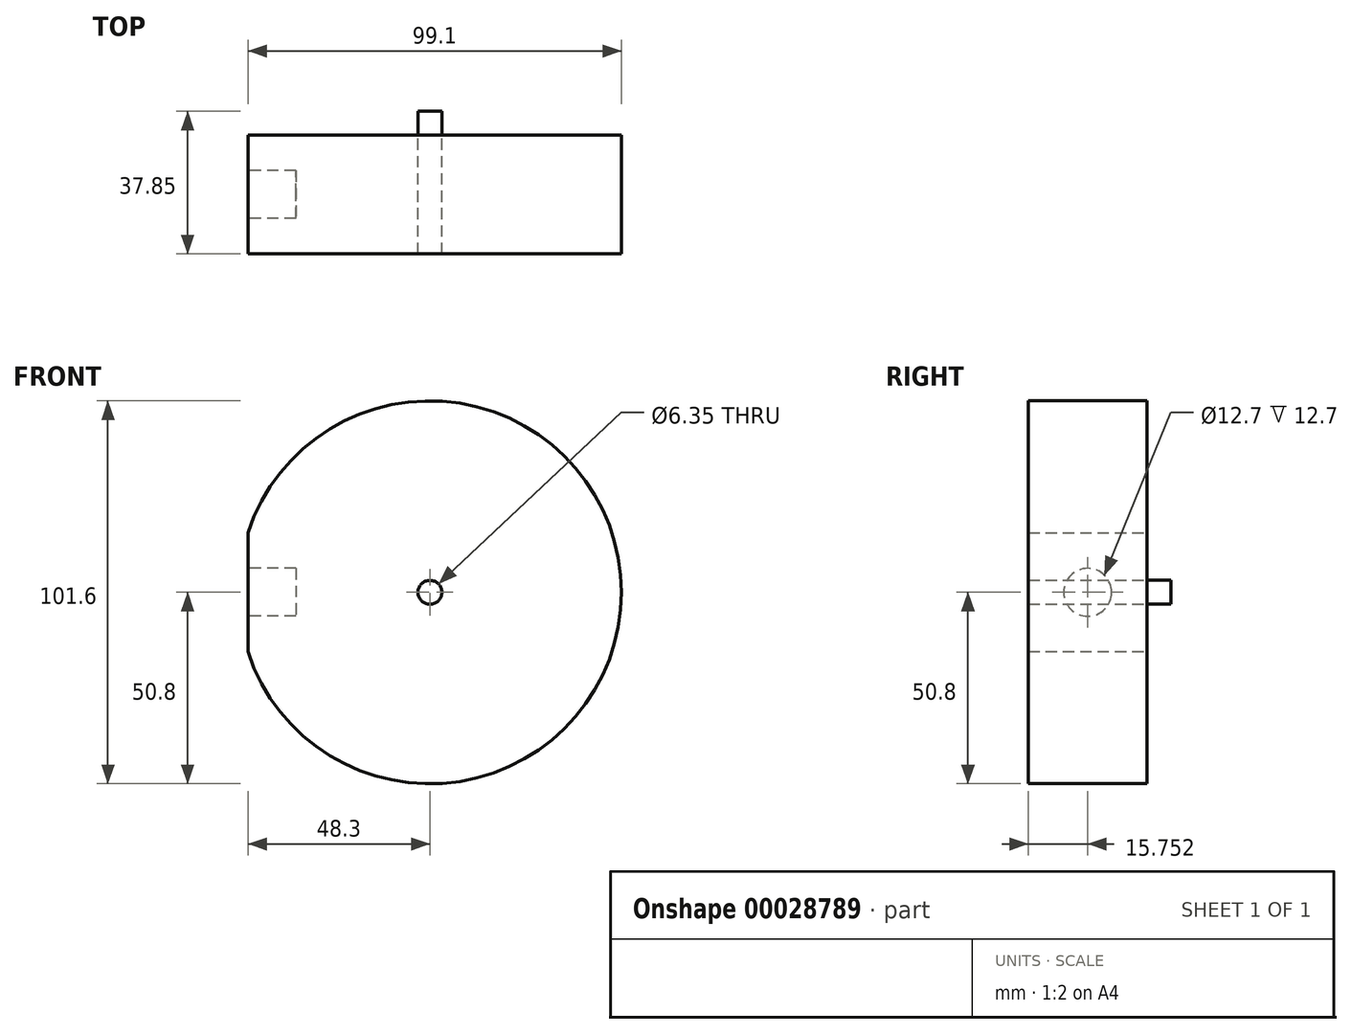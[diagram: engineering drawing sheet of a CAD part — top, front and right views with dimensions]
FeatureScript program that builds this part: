
annotation { "Feature Type Name" : "Feature", "Feature Type Description" : "" }
export const myFeature = defineFeature(function(context is Context, id is Id, definition is map)
    precondition{}
    {
        {
            var Q0;
            Q0=qCreatedBy(makeId("Front.planeOp"),FACE);
            var sketch = newSketch(context, id + "F0", { "sketchPlane" : qUnion([Q0])});
            skArc(sketch, "E0", {"start": v(-48.3, -15.75) * mm, "mid": v(50.8, 0) * mm, "end": v(-48.3, 15.75) * mm});
            skCircle(sketch, "E1", {"center": v(0, 0) * mm, "radius": 3.18 * mm});
            skLineSegment(sketch, "E2", {"start": v(-67.95, 15.75) * mm, "end": v(63.5, 15.75) * mm, "construction": true});
            skLineSegment(sketch, "E3", {"start": v(-67.95, -15.75) * mm, "end": v(63.5, -15.75) * mm, "construction": true});
            skLineSegment(sketch, "E4", {"start": v(0, 0) * mm, "end": v(-103.86, 0) * mm, "construction": true});
            skLineSegment(sketch, "E5", {"start": v(-48.3, 15.75) * mm, "end": v(-48.3, -15.75) * mm});
            skSolve(sketch);
        }
        {
            var Q0;
            Q0=makeQuery(id+"F0.imprint","IMPRINT",FACE,{"disambiguationData":[TD([[makeQuery(id+"F0.imprint","IMPRINT",EDGE,{"derivedFrom":sQuery(id+"F0.wireOp",EDGE,"E0")}),1.0]])]});
            extrude(context, id + "F1", {"entities" : qUnion([Q0]), "depth" : 31.5 * mm});
        }
        {
            var Q0;
            Q0=makeQuery(id+"F1.opExtrude","SWEPT_FACE",FACE,{"disambiguationData":[OSD([sQuery(id+"F0.wireOp",EDGE,"E5")])]});
            var sketch = newSketch(context, id + "F2", { "sketchPlane" : qUnion([Q0])});
            skLineSegment(sketch, "E6", {"start": v(0, 0) * mm, "end": v(31.5, 0) * mm, "construction": true});
            skCircle(sketch, "E7", {"center": v(15.75, 0) * mm, "radius": 6.35 * mm});
            skSolve(sketch);
        }
        {
            var Q0;
            Q0=makeQuery(id+"F2.imprint","IMPRINT",FACE,{"disambiguationData":[TD([[makeQuery(id+"F2.imprint","IMPRINT",EDGE,{"derivedFrom":sQuery(id+"F2.wireOp",EDGE,"E7")}),1.0]])]});
            extrude(context, id + "F3", {"entities" : qUnion([Q0]), "operationType" : NewBodyOperationType.REMOVE, "oppositeDirection" : true, "depth" : 12.7 * mm});
        }
        {
            var Q0;
            Q0=makeQuery(id+"F0.imprint","IMPRINT",FACE,{"disambiguationData":[TD([[makeQuery(id+"F0.imprint","IMPRINT",EDGE,{"derivedFrom":sQuery(id+"F0.wireOp",EDGE,"E1")}),1.0]])]});
            extrude(context, id + "F4", {"entities" : qUnion([Q0]), "oppositeDirection" : true, "depth" : 6.35 * mm});
        }
    });
